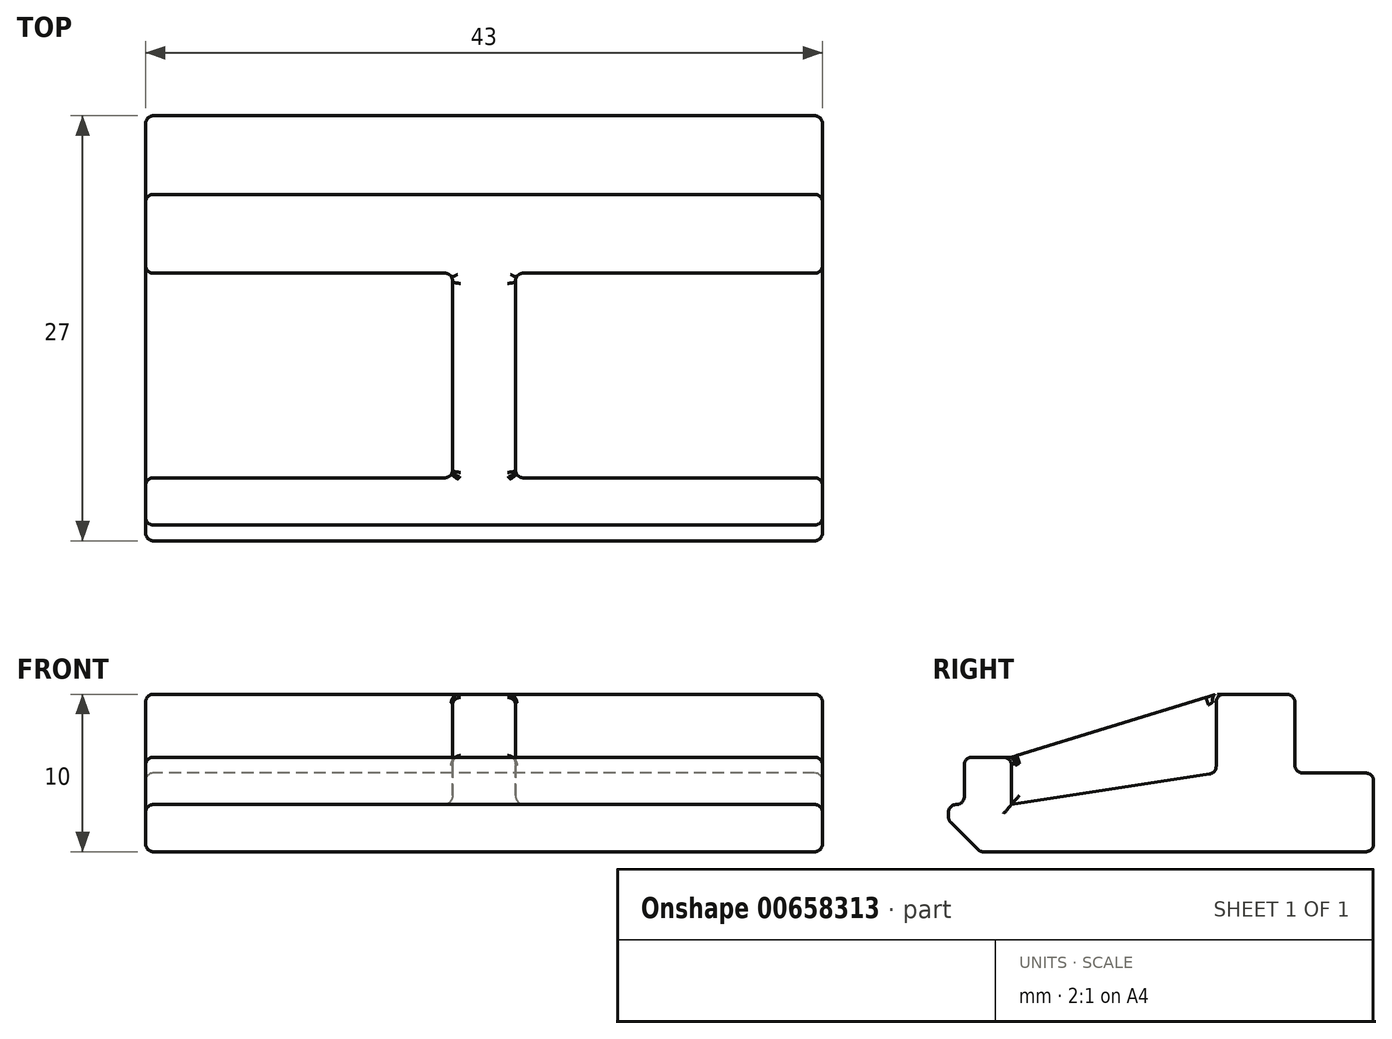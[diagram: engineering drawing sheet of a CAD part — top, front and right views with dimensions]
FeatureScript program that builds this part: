
annotation { "Feature Type Name" : "Feature", "Feature Type Description" : "" }
export const myFeature = defineFeature(function(context is Context, id is Id, definition is map)
    precondition{}
    {
        {
            var Q0;
            Q0=qCreatedBy(makeId("Right.planeOp"),FACE);
            var sketch = newSketch(context, id + "F0", { "sketchPlane" : qUnion([Q0])});
            skLineSegment(sketch, "E0", {"start": v(0, 0) * mm, "end": v(27, 0) * mm});
            skLineSegment(sketch, "E1", {"start": v(27, 0) * mm, "end": v(27, 5) * mm});
            skLineSegment(sketch, "E2", {"start": v(27, 5) * mm, "end": v(22, 5) * mm});
            skLineSegment(sketch, "E3", {"start": v(22, 5) * mm, "end": v(22, 10) * mm});
            skLineSegment(sketch, "E4", {"start": v(22, 10) * mm, "end": v(17, 10) * mm});
            skLineSegment(sketch, "E5", {"start": v(17, 10) * mm, "end": v(17, 5) * mm});
            skLineSegment(sketch, "E6", {"start": v(17, 5) * mm, "end": v(4, 3) * mm});
            skLineSegment(sketch, "E7", {"start": v(4, 3) * mm, "end": v(4, 6) * mm});
            skLineSegment(sketch, "E8", {"start": v(4, 6) * mm, "end": v(1, 6) * mm});
            skLineSegment(sketch, "E9", {"start": v(1, 6) * mm, "end": v(1, 3) * mm});
            skLineSegment(sketch, "E10", {"start": v(1, 3) * mm, "end": v(0, 3) * mm});
            skLineSegment(sketch, "E11", {"start": v(0, 3) * mm, "end": v(0, 0) * mm});
            skSolve(sketch);
        }
        {
            var Q0;
            Q0 = qSketchRegion(id + "F0", true);
            extrude(context, id + "F1", {"entities" : qUnion([Q0]), "endBound" : BoundingType.SYMMETRIC, "depth" : 43 * mm, "offsetDistance" : 25.4 * mm});
        }
        {
            var Q0;
            Q0=qCreatedBy(makeId("Right.planeOp"),FACE);
            var sketch = newSketch(context, id + "F2", { "sketchPlane" : qUnion([Q0])});
            skLineSegment(sketch, "E12", {"start": v(4, 6) * mm, "end": v(17, 10) * mm});
            skLineSegment(sketch, "E13", {"start": v(17, 10) * mm, "end": v(17, 5) * mm});
            skLineSegment(sketch, "E14", {"start": v(17, 5) * mm, "end": v(4, 3) * mm});
            skLineSegment(sketch, "E15", {"start": v(4, 3) * mm, "end": v(4, 6) * mm});
            skSolve(sketch);
        }
        {
            var Q0;
            Q0 = qSketchRegion(id + "F2", true);
            extrude(context, id + "F3", {"entities" : qUnion([Q0]), "operationType" : NewBodyOperationType.ADD, "endBound" : BoundingType.SYMMETRIC, "depth" : 4 * mm, "offsetDistance" : 25.4 * mm});
        }
        {
            var Q0;
            Q0=makeQuery(id+"F1.opExtrude","SWEPT_EDGE",EDGE,{"disambiguationData":[OSD([sQuery(id+"F0.wireOp",EDGE,"E0"),sQuery(id+"F0.wireOp",EDGE,"E11")])]});
            chamfer(context, id + "F4", {"entities" : qUnion([Q0]), "chamferType" : ChamferType.TWO_OFFSETS, "width1" : 2 * mm, "oppositeDirection" : true, "width2" : 2 * mm, "tangentPropagation" : true});
        }
        {
            var Q0;
            Q0=makeQuery(id+"F1.opExtrude","SWEPT_EDGE",EDGE,{"disambiguationData":[OSD([sQuery(id+"F0.wireOp",EDGE,"E9"),sQuery(id+"F0.wireOp",EDGE,"E10")])]});
            var Q1;
            Q1=makeQuery(id+"F1.opExtrude","SWEPT_EDGE",EDGE,{"disambiguationData":[OSD([sQuery(id+"F0.wireOp",EDGE,"E10"),sQuery(id+"F0.wireOp",EDGE,"E11")])]});
            var Q2;
            {var subQ0=sQuery(id+"F0.wireOp",EDGE,"E11");Q2=makeQuery(id+"F4.opChamfer","BLEND_EDGE",EDGE,{"blendedFrom":[makeQuery(id+"F1.opExtrude","SWEPT_EDGE",EDGE,{"disambiguationData":[OSD([sQuery(id+"F0.wireOp",EDGE,"E0"),subQ0])]}),makeQuery(id+"F1.opExtrude","SWEPT_FACE",FACE,{"disambiguationData":[OSD([subQ0])]})],"blendedInto":[makeQuery(id+"F1.opExtrude","SWEPT_FACE",FACE,{"disambiguationData":[OSD([subQ0])]})]});}
            var Q3;
            {var subQ0=sQuery(id+"F0.wireOp",EDGE,"E0");Q3=makeQuery(id+"F4.opChamfer","BLEND_EDGE",EDGE,{"blendedFrom":[makeQuery(id+"F1.opExtrude","SWEPT_EDGE",EDGE,{"disambiguationData":[OSD([subQ0,sQuery(id+"F0.wireOp",EDGE,"E11")])]}),makeQuery(id+"F1.opExtrude","SWEPT_FACE",FACE,{"disambiguationData":[OSD([subQ0])]})],"blendedInto":[makeQuery(id+"F1.opExtrude","SWEPT_FACE",FACE,{"disambiguationData":[OSD([subQ0])]})]});}
            var Q4;
            Q4=makeQuery(id+"F1.opExtrude","CAP_EDGE",EDGE,{"disambiguationData":[OSD([sQuery(id+"F0.wireOp",EDGE,"E0")])],"isStart":true});
            var Q5;
            Q5=makeQuery(id+"F1.opExtrude","CAP_FACE",FACE,{"disambiguationData":[OSD([sQuery(id+"F0.wireOp",EDGE,"E0"),sQuery(id+"F0.wireOp",EDGE,"E1"),sQuery(id+"F0.wireOp",EDGE,"E2"),sQuery(id+"F0.wireOp",EDGE,"E3"),sQuery(id+"F0.wireOp",EDGE,"E4"),sQuery(id+"F0.wireOp",EDGE,"E5"),sQuery(id+"F0.wireOp",EDGE,"E6"),sQuery(id+"F0.wireOp",EDGE,"E7"),sQuery(id+"F0.wireOp",EDGE,"E8"),sQuery(id+"F0.wireOp",EDGE,"E9"),sQuery(id+"F0.wireOp",EDGE,"E10"),sQuery(id+"F0.wireOp",EDGE,"E11")])],"isStart":true});
            var Q6;
            Q6=makeQuery(id+"F1.opExtrude","CAP_FACE",FACE,{"disambiguationData":[OSD([sQuery(id+"F0.wireOp",EDGE,"E0"),sQuery(id+"F0.wireOp",EDGE,"E1"),sQuery(id+"F0.wireOp",EDGE,"E2"),sQuery(id+"F0.wireOp",EDGE,"E3"),sQuery(id+"F0.wireOp",EDGE,"E4"),sQuery(id+"F0.wireOp",EDGE,"E5"),sQuery(id+"F0.wireOp",EDGE,"E6"),sQuery(id+"F0.wireOp",EDGE,"E7"),sQuery(id+"F0.wireOp",EDGE,"E8"),sQuery(id+"F0.wireOp",EDGE,"E9"),sQuery(id+"F0.wireOp",EDGE,"E10"),sQuery(id+"F0.wireOp",EDGE,"E11")])],"isStart":false});
            var Q7;
            Q7=makeQuery(id+"F1.opExtrude","SWEPT_FACE",FACE,{"disambiguationData":[OSD([sQuery(id+"F0.wireOp",EDGE,"E1")])]});
            var Q8;
            Q8=makeQuery(id+"F1.opExtrude","SWEPT_FACE",FACE,{"disambiguationData":[OSD([sQuery(id+"F0.wireOp",EDGE,"E3")])]});
            var Q9;
            Q9=makeQuery(id+"F3.opExtrude","SWEPT_FACE",FACE,{"disambiguationData":[OSD([sQuery(id+"F2.wireOp",EDGE,"E12")])]});
            var Q10;
            {var subQ0=sQuery(id+"F2.wireOp",EDGE,"E12");var subQ3=sQuery(id+"F0.wireOp",EDGE,"E5");Q10=makeQuery(id+"F3.boolean.opBoolean","SPLIT",FACE,{"disambiguationData":[TD([makeQuery(id+"F3.opExtrude","CAP_FACE",FACE,{"disambiguationData":[OSD([subQ0,sQuery(id+"F2.wireOp",EDGE,"E13"),sQuery(id+"F2.wireOp",EDGE,"E14"),sQuery(id+"F2.wireOp",EDGE,"E15")])],"isStart":false})])],"derivedFrom":makeQuery(id+"F1.opExtrude","SWEPT_FACE",FACE,{"disambiguationData":[OSD([subQ3])]})});}
            var Q11;
            {var subQ0=sQuery(id+"F2.wireOp",EDGE,"E12");var subQ2=sQuery(id+"F0.wireOp",EDGE,"E5");Q11=makeQuery(id+"F3.boolean.opBoolean","SPLIT",FACE,{"disambiguationData":[TD([makeQuery(id+"F3.opExtrude","CAP_FACE",FACE,{"disambiguationData":[OSD([subQ0,sQuery(id+"F2.wireOp",EDGE,"E13"),sQuery(id+"F2.wireOp",EDGE,"E14"),sQuery(id+"F2.wireOp",EDGE,"E15")])],"isStart":true})])],"derivedFrom":makeQuery(id+"F1.opExtrude","SWEPT_FACE",FACE,{"disambiguationData":[OSD([subQ2])]})});}
            var Q12;
            Q12=makeQuery(id+"F3.opExtrude","CAP_FACE",FACE,{"disambiguationData":[OSD([sQuery(id+"F2.wireOp",EDGE,"E12"),sQuery(id+"F2.wireOp",EDGE,"E13"),sQuery(id+"F2.wireOp",EDGE,"E14"),sQuery(id+"F2.wireOp",EDGE,"E15")])],"isStart":false});
            var Q13;
            Q13=makeQuery(id+"F1.opExtrude","SWEPT_FACE",FACE,{"disambiguationData":[OSD([sQuery(id+"F0.wireOp",EDGE,"E8")])]});
            var Q14;
            Q14=makeQuery(id+"F3.opExtrude","CAP_FACE",FACE,{"disambiguationData":[OSD([sQuery(id+"F2.wireOp",EDGE,"E12"),sQuery(id+"F2.wireOp",EDGE,"E13"),sQuery(id+"F2.wireOp",EDGE,"E14"),sQuery(id+"F2.wireOp",EDGE,"E15")])],"isStart":true});
            fillet(context, id + "F5", {"entities" : qUnion([Q0, Q1, Q2, Q3, Q4, Q5, Q6, Q7, Q8, Q9, Q10, Q11, Q12, Q13, Q14]), "radius" : .5 * mm, "tangentPropagation" : true, "allowEdgeOverflow" : false});
        }
    });
